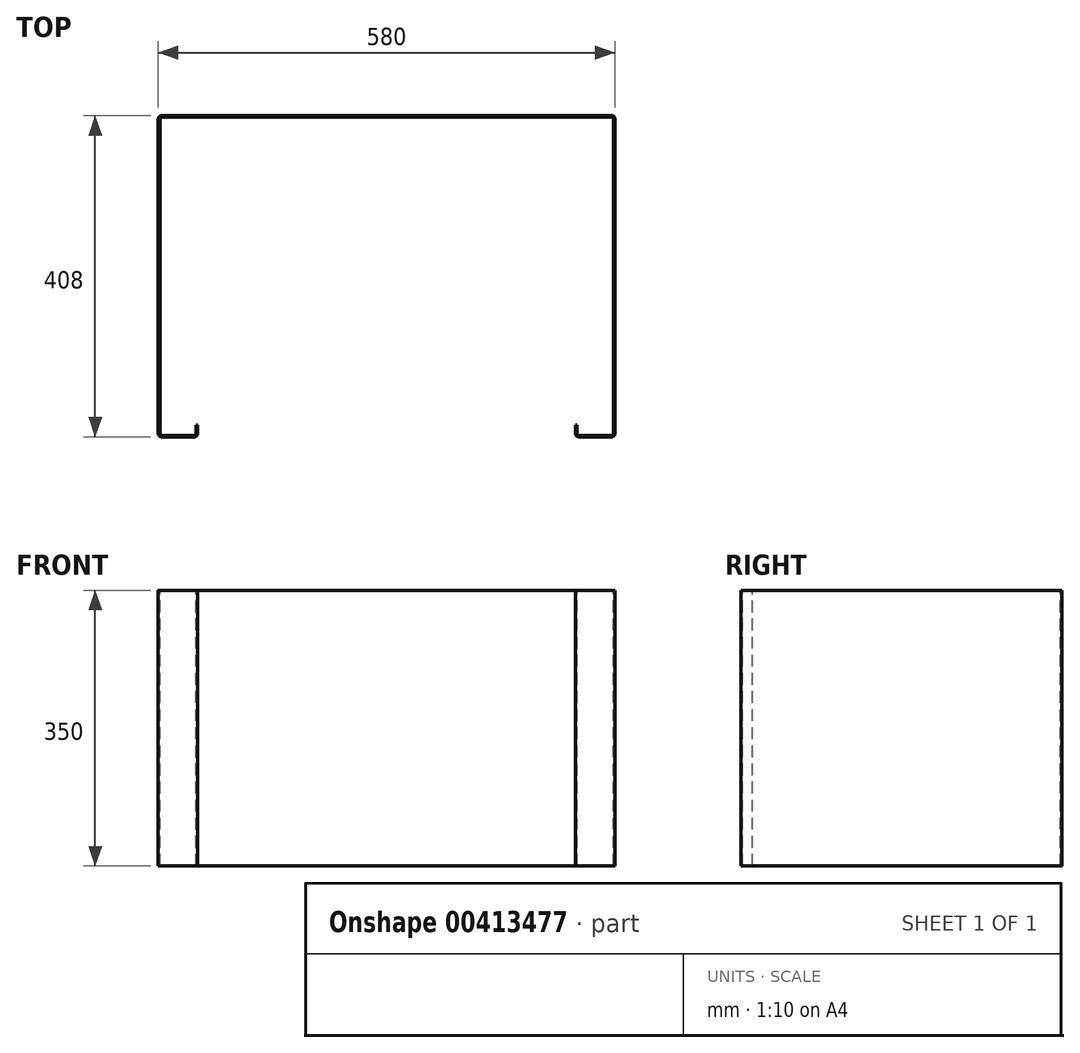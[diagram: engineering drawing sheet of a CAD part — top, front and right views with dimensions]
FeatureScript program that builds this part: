
annotation { "Feature Type Name" : "Feature", "Feature Type Description" : "" }
export const myFeature = defineFeature(function(context is Context, id is Id, definition is map)
    precondition{}
    {
        {
            var Q0;
            Q0=qCreatedBy(makeId("Top.planeOp"),FACE);
            var sketch = newSketch(context, id + "F0", { "sketchPlane" : qUnion([Q0])});
            skLineSegment(sketch, "E0.bottom", {"start": v(-286, 0) * mm, "end": v(-244, 0) * mm});
            skLineSegment(sketch, "E0.top", {"start": v(-286, 408) * mm, "end": v(286, 408) * mm});
            skLineSegment(sketch, "E0.left", {"start": v(-290, 4) * mm, "end": v(-290, 404) * mm});
            skLineSegment(sketch, "E0.right", {"start": v(290, 4) * mm, "end": v(290, 404) * mm});
            skPoint(sketch, "E1.visualSharp", {"position": v(-290, 408) * mm});
            skArc(sketch, "E1.filletArc", {"start": v(-286, 408) * mm, "mid": v(-288.83, 406.83) * mm, "end": v(-290, 404) * mm});
            skPoint(sketch, "E2.visualSharp", {"position": v(-290, 0) * mm});
            skArc(sketch, "E2.filletArc", {"start": v(-290, 4) * mm, "mid": v(-288.83, 1.17) * mm, "end": v(-286, 0) * mm});
            skPoint(sketch, "E3.visualSharp", {"position": v(290, 408) * mm});
            skArc(sketch, "E3.filletArc", {"start": v(290, 404) * mm, "mid": v(288.83, 406.83) * mm, "end": v(286, 408) * mm});
            skPoint(sketch, "E4.visualSharp", {"position": v(290, 0) * mm});
            skArc(sketch, "E4.filletArc", {"start": v(286, 0) * mm, "mid": v(288.83, 1.17) * mm, "end": v(290, 4) * mm});
            skLineSegment(sketch, "E5", {"start": v(244, 0) * mm, "end": v(286, 0) * mm});
            skLineSegment(sketch, "E6", {"start": v(-240, 4) * mm, "end": v(-240, 15) * mm});
            skArc(sketch, "E7.filletArc", {"start": v(-244, 0) * mm, "mid": v(-241.17, 1.17) * mm, "end": v(-240, 4) * mm});
            skLineSegment(sketch, "E8", {"start": v(240, 4) * mm, "end": v(240, 15) * mm});
            skArc(sketch, "E9.filletArc", {"start": v(240, 4) * mm, "mid": v(241.17, 1.17) * mm, "end": v(244, 0) * mm});
            skLineSegment(sketch, "E10.0", {"start": v(-288, 4) * mm, "end": v(-288, 404) * mm});
            skLineSegment(sketch, "E11.0", {"start": v(-286, 406) * mm, "end": v(286, 406) * mm});
            skLineSegment(sketch, "E12.0", {"start": v(288, 4) * mm, "end": v(288, 404) * mm});
            skLineSegment(sketch, "E13.0", {"start": v(244, 2) * mm, "end": v(286, 2) * mm});
            skLineSegment(sketch, "E14.0", {"start": v(-286, 2) * mm, "end": v(-244, 2) * mm});
            skLineSegment(sketch, "E15.0", {"start": v(-242, 4) * mm, "end": v(-242, 15) * mm});
            skLineSegment(sketch, "E16.0", {"start": v(242, 4) * mm, "end": v(242, 15) * mm});
            skArc(sketch, "E17.filletArc", {"start": v(242, 4) * mm, "mid": v(242.59, 2.59) * mm, "end": v(244, 2) * mm});
            skLineSegment(sketch, "E18", {"start": v(240, 15) * mm, "end": v(242, 15) * mm});
            skArc(sketch, "E19.filletArc", {"start": v(286, 2) * mm, "mid": v(287.41, 2.59) * mm, "end": v(288, 4) * mm});
            skArc(sketch, "E20.filletArc", {"start": v(288, 404) * mm, "mid": v(287.41, 405.41) * mm, "end": v(286, 406) * mm});
            skArc(sketch, "E21.filletArc", {"start": v(-286, 406) * mm, "mid": v(-287.41, 405.41) * mm, "end": v(-288, 404) * mm});
            skArc(sketch, "E22.filletArc", {"start": v(-288, 4) * mm, "mid": v(-287.41, 2.59) * mm, "end": v(-286, 2) * mm});
            skLineSegment(sketch, "E23", {"start": v(-240, 15) * mm, "end": v(-242, 15) * mm});
            skArc(sketch, "E24.filletArc", {"start": v(-244, 2) * mm, "mid": v(-242.59, 2.59) * mm, "end": v(-242, 4) * mm});
            skSolve(sketch);
        }
        {
            var Q0;
            Q0 = qSketchRegion(id + "F0", true);
            extrude(context, id + "F1", {"entities" : qUnion([Q0]), "oppositeDirection" : true, "depth" : 350 * mm});
        }
    });
